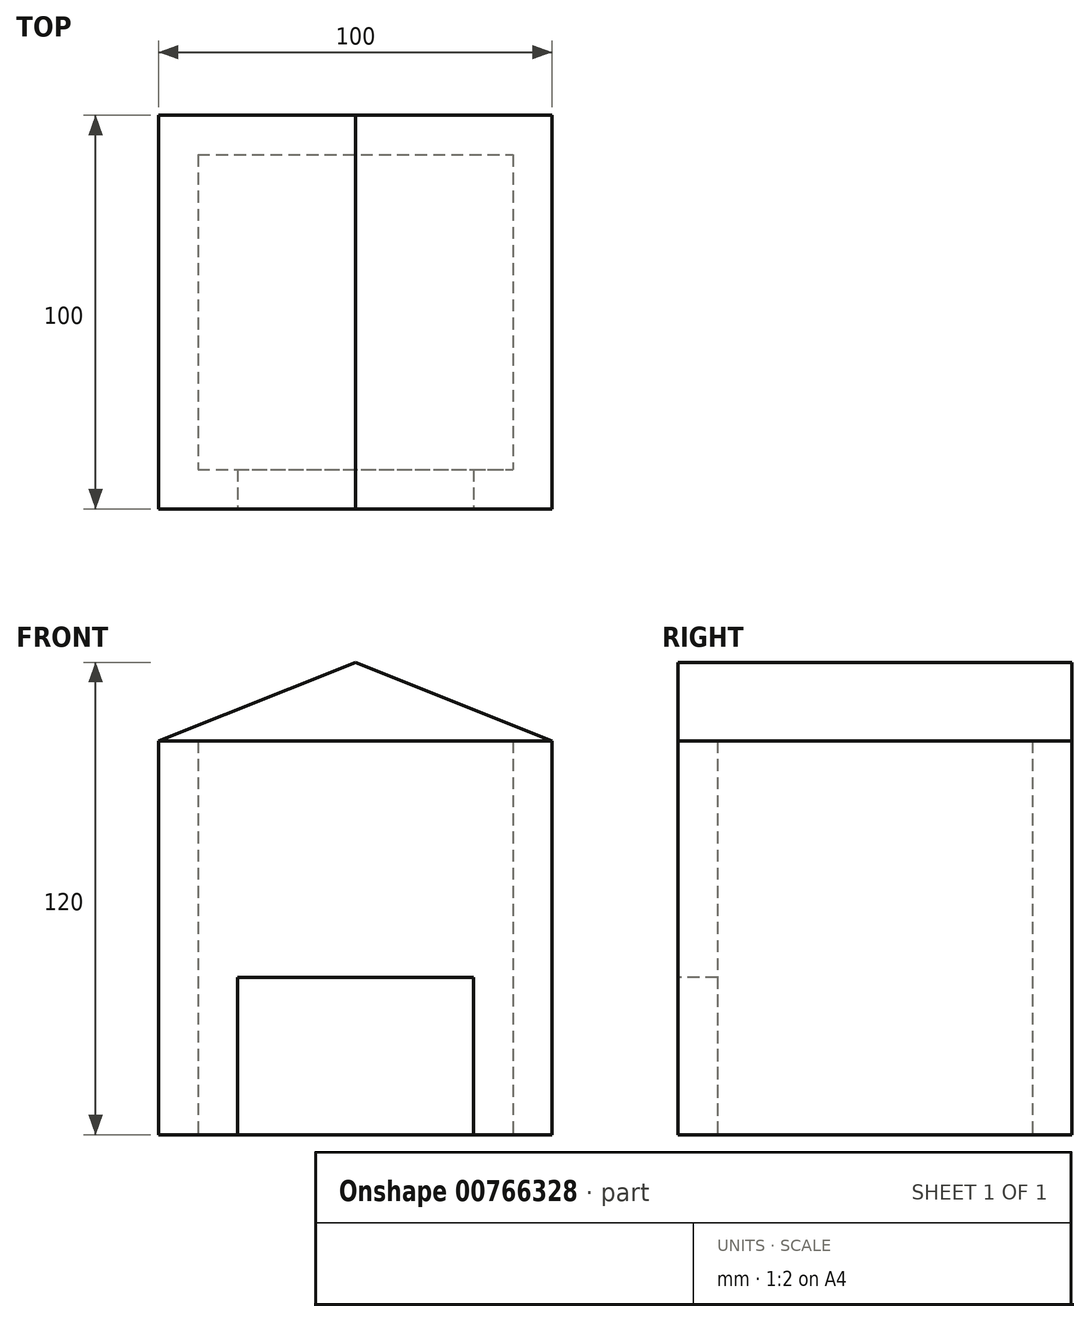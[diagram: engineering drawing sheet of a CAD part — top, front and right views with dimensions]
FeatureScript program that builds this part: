
annotation { "Feature Type Name" : "Feature", "Feature Type Description" : "" }
export const myFeature = defineFeature(function(context is Context, id is Id, definition is map)
    precondition{}
    {
        {
            var Q0;
            Q0=qCreatedBy(makeId("Top.planeOp"),FACE);
            var sketch = newSketch(context, id + "F0", { "sketchPlane" : qUnion([Q0])});
            skLineSegment(sketch, "E0.bottom", {"start": v(-50, 100) * mm, "end": v(50, 100) * mm});
            skLineSegment(sketch, "E0.top", {"start": v(-50, 0) * mm, "end": v(50, 0) * mm});
            skLineSegment(sketch, "E0.left", {"start": v(-50, 100) * mm, "end": v(-50, 0) * mm});
            skLineSegment(sketch, "E0.right", {"start": v(50, 100) * mm, "end": v(50, 0) * mm});
            skLineSegment(sketch, "E1.0", {"start": v(-40, 90) * mm, "end": v(-40, 10) * mm});
            skLineSegment(sketch, "E1.1", {"start": v(-40, 90) * mm, "end": v(40, 90) * mm});
            skLineSegment(sketch, "E1.2", {"start": v(40, 90) * mm, "end": v(40, 10) * mm});
            skLineSegment(sketch, "E1.3", {"start": v(-40, 10) * mm, "end": v(40, 10) * mm});
            skSolve(sketch);
        }
        {
            var Q0;
            Q0=makeQuery(id+"F0.imprint","IMPRINT",FACE,{"disambiguationData":[TD([[makeQuery(id+"F0.imprint","IMPRINT",EDGE,{"derivedFrom":sQuery(id+"F0.wireOp",EDGE,"E0.bottom")}),-1.0]])]});
            extrude(context, id + "F1", {"entities" : qUnion([Q0]), "depth" : 100 * mm, "offsetDistance" : 25 * mm});
        }
        {
            var Q0;
            Q0=makeQuery(id+"F1.opExtrude","SWEPT_FACE",FACE,{"disambiguationData":[OSD([sQuery(id+"F0.wireOp",EDGE,"E0.top")])]});
            var sketch = newSketch(context, id + "F2", { "sketchPlane" : qUnion([Q0])});
            skLineSegment(sketch, "E2.bottom", {"start": v(-30, 40) * mm, "end": v(30, 40) * mm});
            skLineSegment(sketch, "E2.top", {"start": v(-30, 0) * mm, "end": v(30, 0) * mm});
            skLineSegment(sketch, "E2.left", {"start": v(-30, 40) * mm, "end": v(-30, 0) * mm});
            skLineSegment(sketch, "E2.right", {"start": v(30, 40) * mm, "end": v(30, 0) * mm});
            skSolve(sketch);
        }
        {
            var Q0;
            Q0 = qSketchRegion(id + "F2", true);
            extrude(context, id + "F3", {"entities" : qUnion([Q0]), "operationType" : NewBodyOperationType.REMOVE, "endBound" : BoundingType.UP_TO_NEXT, "oppositeDirection" : true, "depth" : 25 * mm, "offsetDistance" : 25 * mm});
        }
        {
            var Q0;
            Q0=makeQuery(id+"F1.opExtrude","SWEPT_FACE",FACE,{"disambiguationData":[OSD([sQuery(id+"F0.wireOp",EDGE,"E0.top")])]});
            var sketch = newSketch(context, id + "F4", { "sketchPlane" : qUnion([Q0])});
            skLineSegment(sketch, "E3", {"start": v(-50, 100) * mm, "end": v(0, 120) * mm});
            skLineSegment(sketch, "E4", {"start": v(0, 120) * mm, "end": v(50, 100) * mm});
            skLineSegment(sketch, "E5", {"start": v(50, 100) * mm, "end": v(-50, 100) * mm});
            skLineSegment(sketch, "E6", {"start": v(0, 100) * mm, "end": v(0, 120) * mm, "construction": true});
            skSolve(sketch);
        }
        {
            var Q0;
            Q0 = qSketchRegion(id + "F4", true);
            var Q1;
            Q1=makeQuery(id+"F1.opExtrude","SWEPT_FACE",FACE,{"disambiguationData":[OSD([sQuery(id+"F0.wireOp",EDGE,"E0.bottom")])]});
            extrude(context, id + "F5", {"entities" : qUnion([Q0]), "endBound" : BoundingType.UP_TO_SURFACE, "oppositeDirection" : true, "depth" : 119.5 * mm, "endBoundEntityFace" : qUnion([Q1]), "offsetDistance" : 25 * mm});
        }
    });
